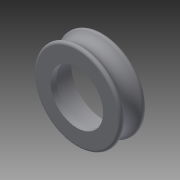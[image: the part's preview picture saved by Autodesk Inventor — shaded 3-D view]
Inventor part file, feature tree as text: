
AUTODESK INVENTOR PART (.ipt)
format: ipt  version: 2014 (Build 180170000, 170)  size: 153,088 bytes
history: native  units: in
note: dims shown in document units (in); Inventor stores cm internally (conversion verified against a paired STEP export)
features: revolve x1
ambient origin geometry x8: Origin, YZ Plane, XZ Plane, XY Plane, X Axis, Y Axis, Z Axis, Center Point
bodies: Solid1 (feature_tree)
feature tree (1):
  revolve  "Revolution1"  [1 undecoded]
note: 1 required parameter value undecoded (feature->parameter linkage not recoverable at this tier; creation-order binding heuristic only, values carry confidence <= 0.55)
